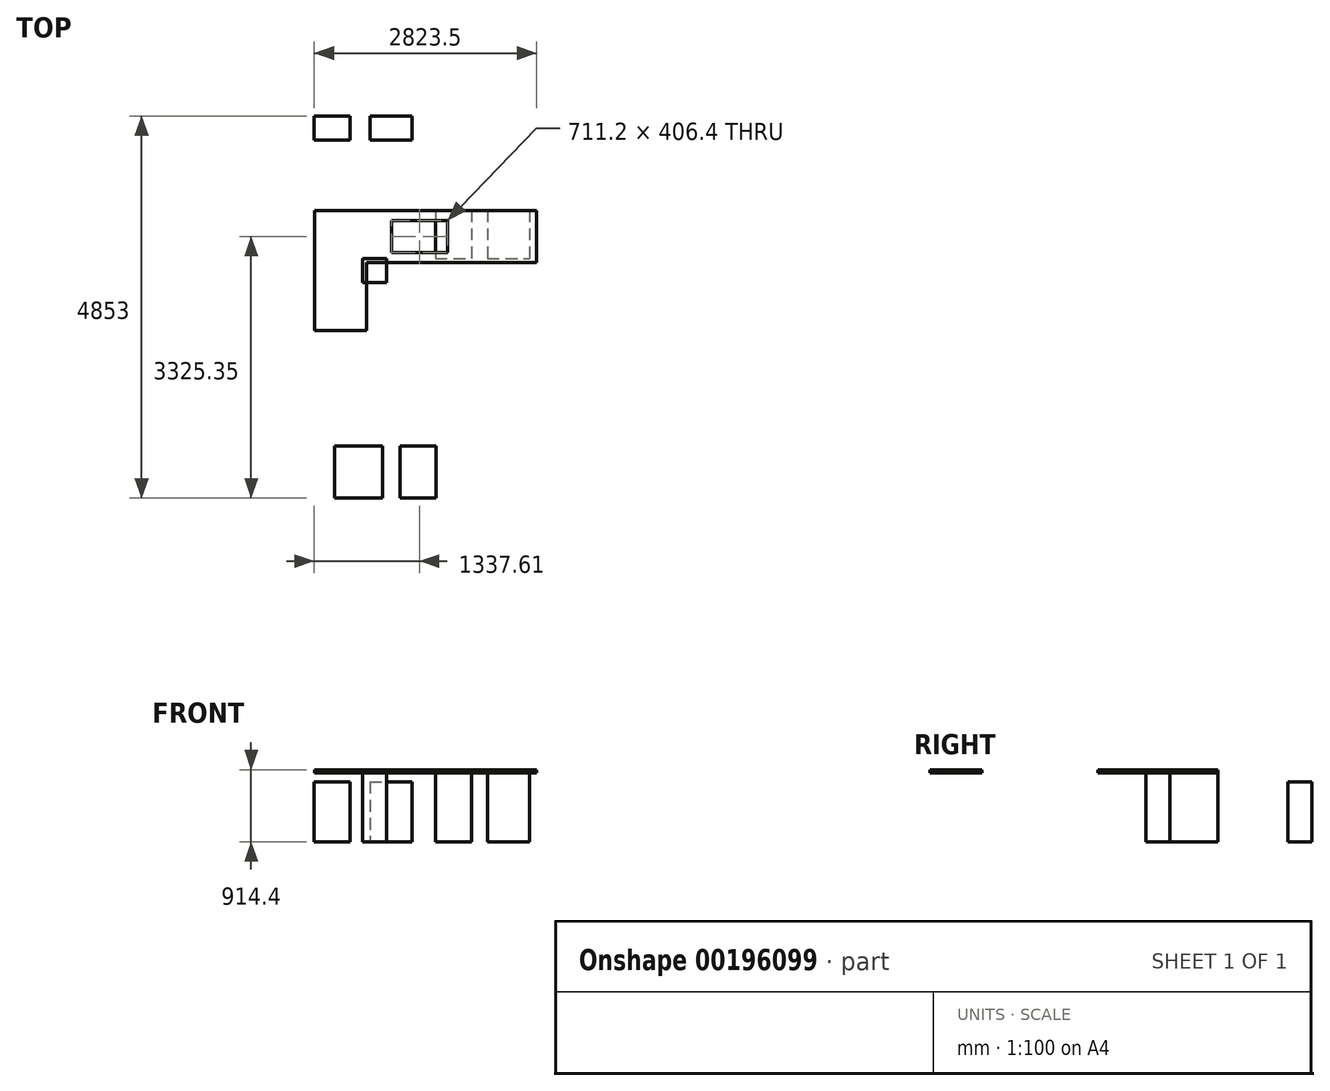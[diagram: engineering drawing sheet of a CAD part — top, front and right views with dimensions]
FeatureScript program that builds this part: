
annotation { "Feature Type Name" : "Feature", "Feature Type Description" : "" }
export const myFeature = defineFeature(function(context is Context, id is Id, definition is map)
    precondition{}
    {
        {
            var Q0;
            Q0=qCreatedBy(makeId("Top.planeOp"),FACE);
            var sketch = newSketch(context, id + "F0", { "sketchPlane" : qUnion([Q0])});
            skLineSegment(sketch, "E0.bottom", {"start": v(4.1, 0) * mm, "end": v(918.5, 0) * mm});
            skLineSegment(sketch, "E0.top", {"start": v(4.1, -914.4) * mm, "end": v(918.5, -914.4) * mm});
            skLineSegment(sketch, "E0.left", {"start": v(4.1, 0) * mm, "end": v(4.1, -914.4) * mm});
            skLineSegment(sketch, "E0.right", {"start": v(918.5, 0) * mm, "end": v(918.5, -914.4) * mm});
            skLineSegment(sketch, "E1.bottom", {"start": v(613.7, -914.4) * mm, "end": v(918.5, -914.4) * mm});
            skLineSegment(sketch, "E1.top", {"start": v(613.7, -609.6) * mm, "end": v(918.5, -609.6) * mm});
            skLineSegment(sketch, "E1.left", {"start": v(613.7, -914.4) * mm, "end": v(613.7, -609.6) * mm});
            skLineSegment(sketch, "E1.right", {"start": v(918.5, -914.4) * mm, "end": v(918.5, -609.6) * mm});
            skCircle(sketch, "E2", {"center": v(461.3, -457.2) * mm, "radius": 406.4 * mm, "construction": true});
            skPoint(sketch, "E2.centerSnap0", {"position": v(461.3, 0) * mm});
            skPoint(sketch, "E2.centerSnap1", {"position": v(4.1, -457.2) * mm});
            skLineSegment(sketch, "E3.bottom", {"start": v(1539.62, 0) * mm, "end": v(1996.82, 0) * mm});
            skLineSegment(sketch, "E3.top", {"start": v(1539.62, -609.6) * mm, "end": v(1996.82, -609.6) * mm});
            skLineSegment(sketch, "E3.left", {"start": v(1539.62, 0) * mm, "end": v(1539.62, -609.6) * mm});
            skLineSegment(sketch, "E3.right", {"start": v(1996.82, 0) * mm, "end": v(1996.82, -609.6) * mm});
            skLineSegment(sketch, "E4.bottom", {"start": v(2200.08, 0) * mm, "end": v(2733.48, 0) * mm});
            skLineSegment(sketch, "E4.top", {"start": v(2200.08, -609.6) * mm, "end": v(2733.48, -609.6) * mm});
            skLineSegment(sketch, "E4.left", {"start": v(2200.08, 0) * mm, "end": v(2200.08, -609.6) * mm});
            skLineSegment(sketch, "E4.right", {"start": v(2733.48, 0) * mm, "end": v(2733.48, -609.6) * mm});
            skLineSegment(sketch, "E5.bottom", {"start": v(0, 1197.45) * mm, "end": v(457.2, 1197.45) * mm});
            skLineSegment(sketch, "E5.top", {"start": v(0, 892.65) * mm, "end": v(457.2, 892.65) * mm});
            skLineSegment(sketch, "E5.left", {"start": v(0, 1197.45) * mm, "end": v(0, 892.65) * mm});
            skLineSegment(sketch, "E5.right", {"start": v(457.2, 1197.45) * mm, "end": v(457.2, 892.65) * mm});
            skLineSegment(sketch, "E6.bottom", {"start": v(707.44, 1197.45) * mm, "end": v(1240.84, 1197.45) * mm});
            skLineSegment(sketch, "E6.top", {"start": v(707.44, 892.65) * mm, "end": v(1240.84, 892.65) * mm});
            skLineSegment(sketch, "E6.left", {"start": v(707.44, 1197.45) * mm, "end": v(707.44, 892.65) * mm});
            skLineSegment(sketch, "E6.right", {"start": v(1240.84, 1197.45) * mm, "end": v(1240.84, 892.65) * mm});
            skSolve(sketch);
        }
        {
            var Q0;
            {var subQ2=sQuery(id+"F0.wireOp",EDGE,"E0.top");Q0=makeQuery(id+"F0.imprint","IMPRINT",FACE,{"disambiguationData":[TD([[makeQuery(id+"F0.imprint","IMPRINT",EDGE,{"derivedFrom":subQ2}),1.0]])]});}
            var Q1;
            Q1=makeQuery(id+"F0.imprint","IMPRINT",FACE,{"disambiguationData":[TD([[makeQuery(id+"F0.imprint","IMPRINT",EDGE,{"derivedFrom":sQuery(id+"F0.wireOp",EDGE,"E3.bottom")}),-1.0]])]});
            var Q2;
            Q2=makeQuery(id+"F0.imprint","IMPRINT",FACE,{"disambiguationData":[TD([[makeQuery(id+"F0.imprint","IMPRINT",EDGE,{"derivedFrom":sQuery(id+"F0.wireOp",EDGE,"E4.bottom")}),-1.0]])]});
            extrude(context, id + "F1", {"entities" : qUnion([Q0, Q1, Q2]), "depth" : 876.3 * mm});
        }
        {
            var Q0;
            Q0=makeQuery(id+"F0.imprint","IMPRINT",FACE,{"disambiguationData":[TD([[makeQuery(id+"F0.imprint","IMPRINT",EDGE,{"derivedFrom":sQuery(id+"F0.wireOp",EDGE,"E5.bottom")}),-1.0]])]});
            var Q1;
            Q1=makeQuery(id+"F0.imprint","IMPRINT",FACE,{"disambiguationData":[TD([[makeQuery(id+"F0.imprint","IMPRINT",EDGE,{"derivedFrom":sQuery(id+"F0.wireOp",EDGE,"E6.bottom")}),-1.0]])]});
            extrude(context, id + "F2", {"entities" : qUnion([Q0, Q1]), "depth" : 762 * mm});
        }
        {
            var Q0;
            Q0=makeQuery(id+"F1.opExtrude","CAP_FACE",FACE,{"disambiguationData":[OSD([sQuery(id+"F0.wireOp",EDGE,"E0.bottom"),sQuery(id+"F0.wireOp",EDGE,"E0.top"),sQuery(id+"F0.wireOp",EDGE,"E0.left"),sQuery(id+"F0.wireOp",EDGE,"E0.right"),sQuery(id+"F0.wireOp",EDGE,"E1.top"),sQuery(id+"F0.wireOp",EDGE,"E1.left")])],"isStart":false});
            var sketch = newSketch(context, id + "F3", { "sketchPlane" : qUnion([Q0])});
            skLineSegment(sketch, "E7", {"start": v(4.1, 0) * mm, "end": v(2823.5, 0) * mm});
            skLineSegment(sketch, "E8", {"start": v(2823.5, 0) * mm, "end": v(2823.5, -660.4) * mm});
            skLineSegment(sketch, "E9", {"start": v(2823.5, -660.4) * mm, "end": v(664.5, -660.4) * mm});
            skLineSegment(sketch, "E10", {"start": v(664.5, -660.4) * mm, "end": v(664.5, -1524) * mm});
            skLineSegment(sketch, "E11.bottom", {"start": v(982, -127) * mm, "end": v(1693.2, -127) * mm});
            skLineSegment(sketch, "E11.top", {"start": v(982, -533.4) * mm, "end": v(1693.2, -533.4) * mm});
            skLineSegment(sketch, "E11.left", {"start": v(982, -127) * mm, "end": v(982, -533.4) * mm});
            skLineSegment(sketch, "E11.right", {"start": v(1693.2, -127) * mm, "end": v(1693.2, -533.4) * mm});
            skLineSegment(sketch, "E12", {"start": v(4.1, 0) * mm, "end": v(4.1, -1524) * mm});
            skLineSegment(sketch, "E13", {"start": v(4.1, -1524) * mm, "end": v(664.5, -1524) * mm});
            skLineSegment(sketch, "E14", {"start": v(1337.6, -127) * mm, "end": v(1337.6, -533.4) * mm, "construction": true});
            skLineSegment(sketch, "E15.bottom", {"start": v(259.81, -2995.15) * mm, "end": v(869.41, -2995.15) * mm});
            skLineSegment(sketch, "E15.top", {"start": v(259.81, -3655.55) * mm, "end": v(869.41, -3655.55) * mm});
            skLineSegment(sketch, "E15.left", {"start": v(259.81, -2995.15) * mm, "end": v(259.81, -3655.55) * mm});
            skLineSegment(sketch, "E15.right", {"start": v(869.41, -2995.15) * mm, "end": v(869.41, -3655.55) * mm});
            skLineSegment(sketch, "E16.bottom", {"start": v(1091.25, -2995.15) * mm, "end": v(1548.45, -2995.15) * mm});
            skLineSegment(sketch, "E16.top", {"start": v(1091.25, -3655.55) * mm, "end": v(1548.45, -3655.55) * mm});
            skLineSegment(sketch, "E16.left", {"start": v(1091.25, -2995.15) * mm, "end": v(1091.25, -3655.55) * mm});
            skLineSegment(sketch, "E16.right", {"start": v(1548.45, -2995.15) * mm, "end": v(1548.45, -3655.55) * mm});
            skSolve(sketch);
        }
        {
            var Q0;
            {var subQ2=sQuery(id+"F3.wireOp",EDGE,"E8");Q0=makeQuery(id+"F3.imprint","IMPRINT",FACE,{"disambiguationData":[TD([[makeQuery(id+"F3.imprint","IMPRINT",EDGE,{"derivedFrom":subQ2}),-1.0]])]});}
            var Q1;
            Q1=makeQuery(id+"F3.imprint","IMPRINT",FACE,{"disambiguationData":[TD([[makeQuery(id+"F3.imprint","IMPRINT",EDGE,{"derivedFrom":makeQuery(id+"F1.opExtrude","CAP_EDGE",EDGE,{"disambiguationData":[OSD([sQuery(id+"F0.wireOp",EDGE,"E0.top")])],"isStart":false})}),1.0]])]});
            var Q2;
            Q2=makeQuery(id+"F3.imprint","IMPRINT",FACE,{"disambiguationData":[TD([[makeQuery(id+"F3.imprint","IMPRINT",EDGE,{"derivedFrom":sQuery(id+"F3.wireOp",EDGE,"E15.bottom")}),-1.0]])]});
            var Q3;
            Q3=makeQuery(id+"F3.imprint","IMPRINT",FACE,{"disambiguationData":[TD([[makeQuery(id+"F3.imprint","IMPRINT",EDGE,{"derivedFrom":sQuery(id+"F3.wireOp",EDGE,"E16.bottom")}),-1.0]])]});
            extrude(context, id + "F4", {"entities" : qUnion([Q0, Q1, Q2, Q3]), "depth" : 38.1 * mm});
        }
    });
